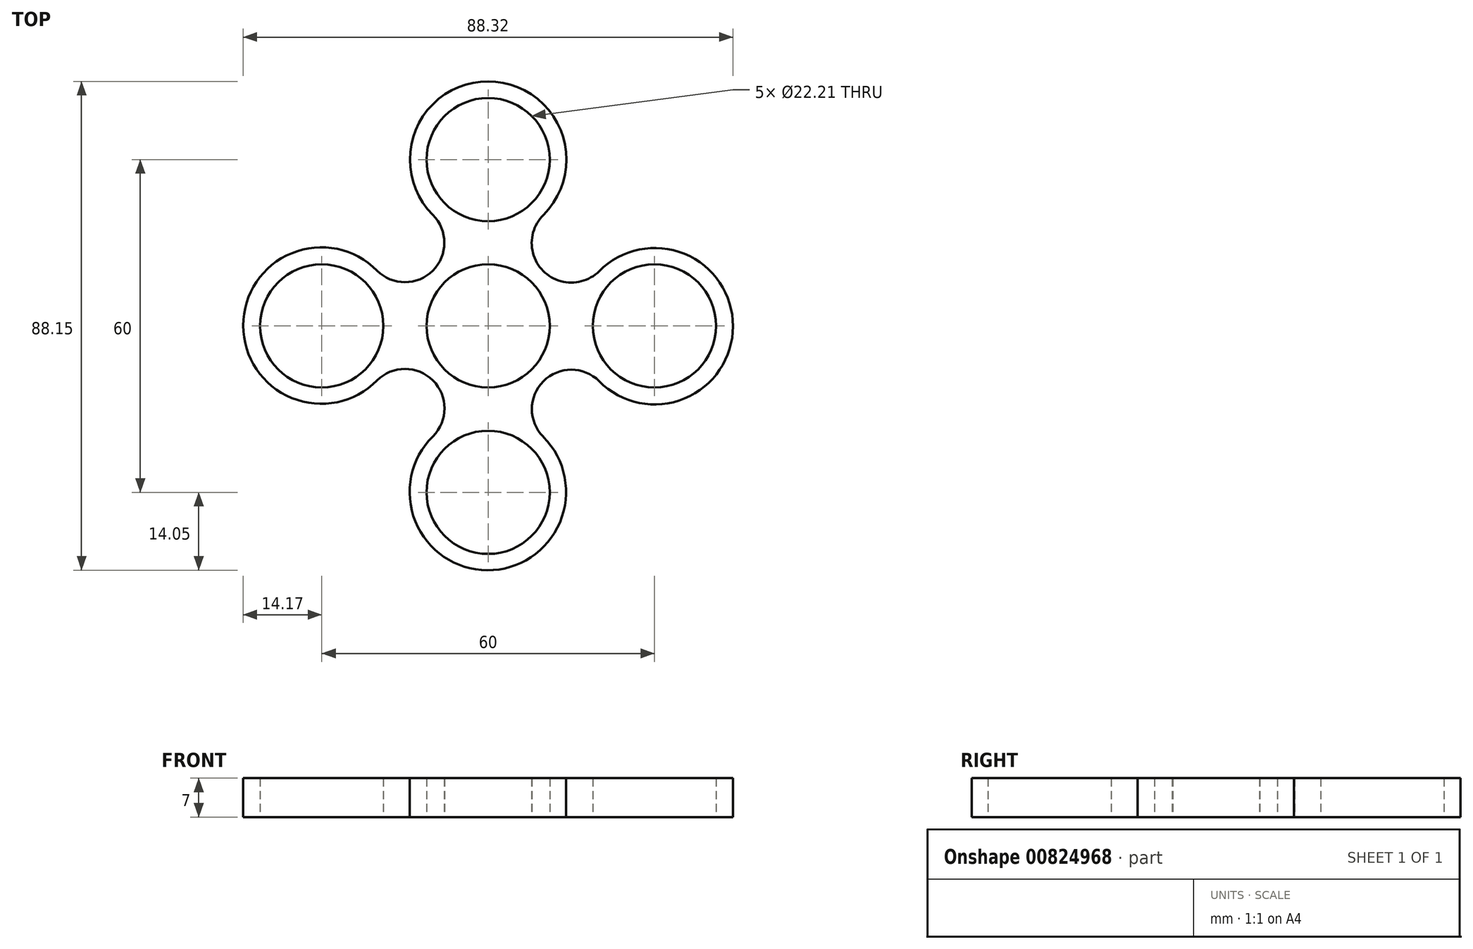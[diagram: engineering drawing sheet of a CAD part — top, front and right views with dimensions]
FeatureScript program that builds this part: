
annotation { "Feature Type Name" : "Feature", "Feature Type Description" : "" }
export const myFeature = defineFeature(function(context is Context, id is Id, definition is map)
    precondition{}
    {
        {
            var Q0;
            Q0=qCreatedBy(makeId("Top.planeOp"),FACE);
            var sketch = newSketch(context, id + "F0", { "sketchPlane" : qUnion([Q0])});
            skCircle(sketch, "E0", {"center": v(0, 30) * mm, "radius": 11.1 * mm});
            skCircle(sketch, "E1.1.0", {"center": v(-30, 0) * mm, "radius": 11.1 * mm});
            skCircle(sketch, "E1.2.0", {"center": v(0, -30) * mm, "radius": 11.1 * mm});
            skPoint(sketch, "E1.center", {"position": v(0, 0) * mm});
            skCircle(sketch, "E2.1.3.0", {"center": v(30, 0) * mm, "radius": 11.1 * mm});
            skCircle(sketch, "E3", {"center": v(0, 0) * mm, "radius": 11.1 * mm});
            skArc(sketch, "E4", {"start": v(-9.96, -19.9) * mm, "mid": v(-9.96, -9.83) * mm, "end": v(-20.03, -9.83) * mm});
            skArc(sketch, "E5", {"start": v(-9.96, -19.9) * mm, "mid": v(-0.14, -44.05) * mm, "end": v(9.97, -20.03) * mm});
            skArc(sketch, "E6", {"start": v(-20.03, 9.97) * mm, "mid": v(-44.17, 0.07) * mm, "end": v(-20.03, -9.83) * mm});
            skArc(sketch, "E7", {"start": v(-20.03, 9.97) * mm, "mid": v(-9.97, 9.97) * mm, "end": v(-9.97, 20.03) * mm});
            skArc(sketch, "E8", {"start": v(9.97, 20.03) * mm, "mid": v(9.93, 9.93) * mm, "end": v(20.03, 9.88) * mm});
            skArc(sketch, "E9", {"start": v(20.03, -9.97) * mm, "mid": v(9.97, -9.97) * mm, "end": v(9.97, -20.03) * mm});
            skArc(sketch, "E10", {"start": v(9.97, 20.03) * mm, "mid": v(0, 44.1) * mm, "end": v(-9.97, 20.03) * mm});
            skArc(sketch, "E11", {"start": v(20.03, -9.97) * mm, "mid": v(44.15, -0.05) * mm, "end": v(20.03, 9.88) * mm});
            skSolve(sketch);
        }
        {
            var Q0;
            Q0=makeQuery(id+"F0.imprint","IMPRINT",FACE,{"disambiguationData":[TD([[makeQuery(id+"F0.imprint","IMPRINT",EDGE,{"derivedFrom":sQuery(id+"F0.wireOp",EDGE,"E0")}),-1.0]])]});
            extrude(context, id + "F1", {"entities" : qUnion([Q0]), "depth" : 7 * mm, "offsetDistance" : 25 * mm});
        }
    });
